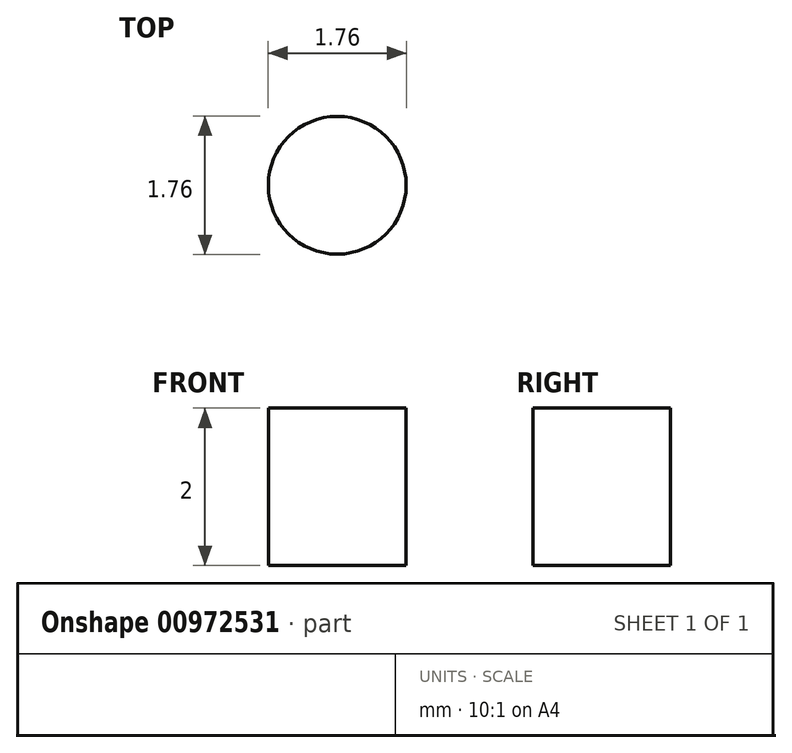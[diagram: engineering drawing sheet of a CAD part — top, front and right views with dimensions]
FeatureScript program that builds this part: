
annotation { "Feature Type Name" : "Feature", "Feature Type Description" : "" }
export const myFeature = defineFeature(function(context is Context, id is Id, definition is map)
    precondition{}
    {
        {
            var Q0;
            Q0=qCreatedBy(makeId("Top.planeOp"),FACE);
            var sketch = newSketch(context, id + "F0", { "sketchPlane" : qUnion([Q0])});
            skCircle(sketch, "E0", {"center": v(0, 0) * mm, "radius": 0.87 * mm});
            skSolve(sketch);
        }
        {
            var Q0;
            Q0 = qSketchRegion(id + "F0", true);
            extrude(context, id + "F1", {"entities" : qUnion([Q0]), "depth" : 2 * mm, "offsetDistance" : 25.4 * mm});
        }
    });
